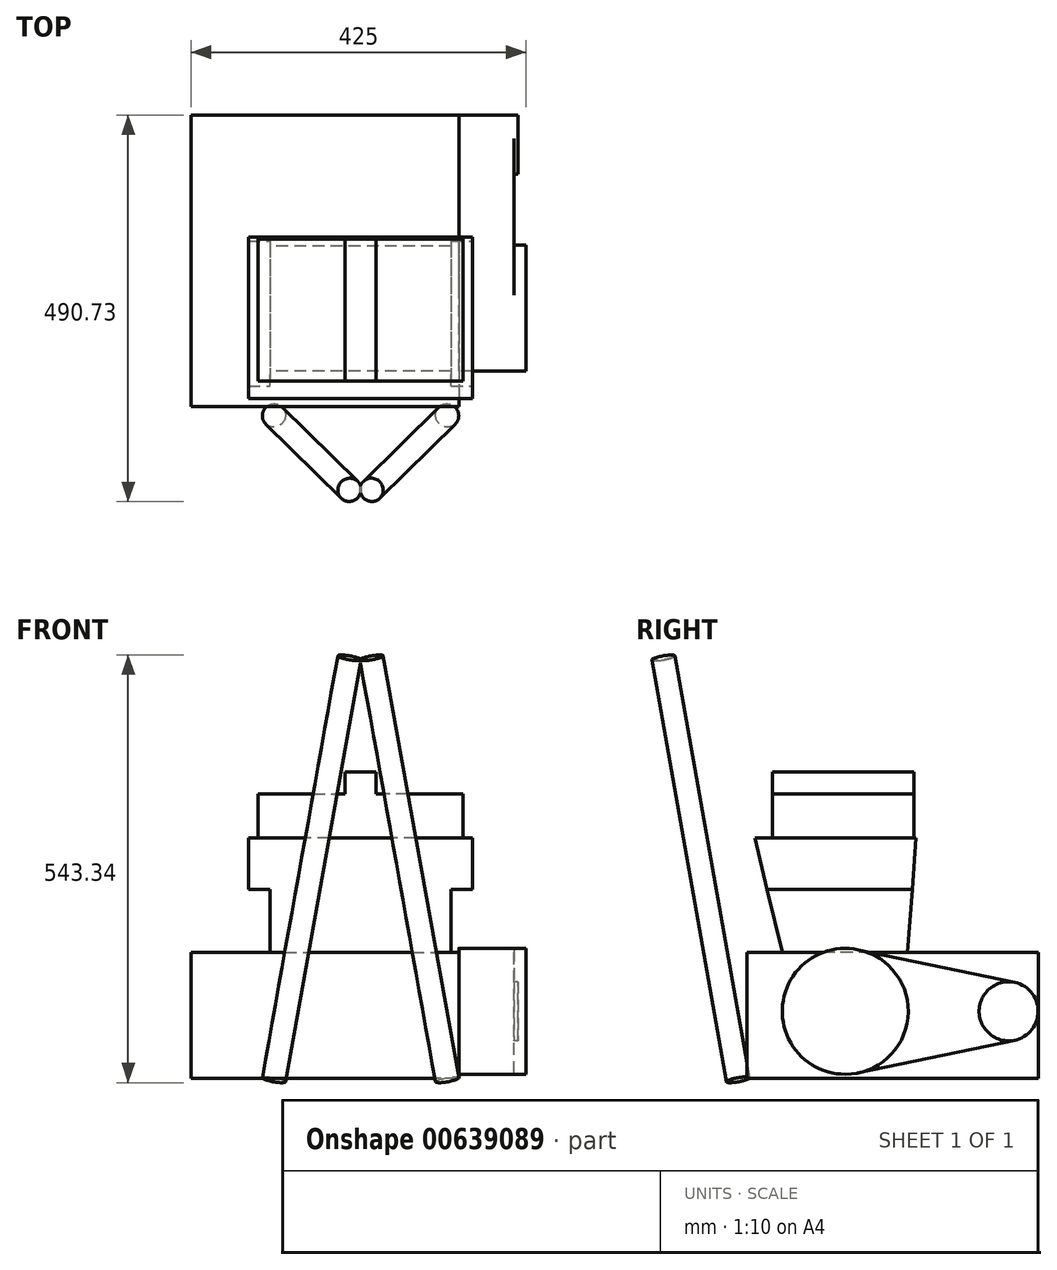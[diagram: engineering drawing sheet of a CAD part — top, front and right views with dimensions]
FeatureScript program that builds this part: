
annotation { "Feature Type Name" : "Feature", "Feature Type Description" : "" }
export const myFeature = defineFeature(function(context is Context, id is Id, definition is map)
    precondition{}
    {
        {
            var Q0;
            Q0=qCreatedBy(makeId("Front.planeOp"),FACE);
            var sketch = newSketch(context, id + "F0", { "sketchPlane" : qUnion([Q0])});
            skLineSegment(sketch, "E0", {"start": v(-215, 0) * mm, "end": v(115, 0) * mm});
            skLineSegment(sketch, "E1", {"start": v(-215, 0) * mm, "end": v(-215, 160) * mm});
            skLineSegment(sketch, "E2", {"start": v(-215, 160) * mm, "end": v(115, 160) * mm});
            skLineSegment(sketch, "E3", {"start": v(-115, 160) * mm, "end": v(-115, 240) * mm});
            skLineSegment(sketch, "E4", {"start": v(115, 160) * mm, "end": v(115, 240) * mm});
            skLineSegment(sketch, "E5", {"start": v(-115, 240) * mm, "end": v(115, 240) * mm});
            skLineSegment(sketch, "E6", {"start": v(-115, 240) * mm, "end": v(-142.5, 240) * mm});
            skLineSegment(sketch, "E7", {"start": v(-142.5, 240) * mm, "end": v(-142.5, 305) * mm});
            skLineSegment(sketch, "E8", {"start": v(-142.5, 305) * mm, "end": v(142.5, 305) * mm});
            skLineSegment(sketch, "E9", {"start": v(142.5, 305) * mm, "end": v(142.5, 240) * mm});
            skLineSegment(sketch, "E10", {"start": v(142.5, 240) * mm, "end": v(115, 240) * mm});
            skLineSegment(sketch, "E11", {"start": v(0, 540.42) * mm, "end": v(0, 0) * mm, "construction": true});
            skLineSegment(sketch, "E12", {"start": v(-130, 305) * mm, "end": v(-130, 361) * mm});
            skLineSegment(sketch, "E13", {"start": v(-20, 389) * mm, "end": v(20, 389) * mm});
            skLineSegment(sketch, "E14", {"start": v(130, 361) * mm, "end": v(130, 305) * mm});
            skLineSegment(sketch, "E15", {"start": v(-130, 361) * mm, "end": v(-20, 361) * mm});
            skLineSegment(sketch, "E16", {"start": v(-20, 361) * mm, "end": v(-20, 389) * mm});
            skLineSegment(sketch, "E17", {"start": v(130, 361) * mm, "end": v(20, 361) * mm});
            skLineSegment(sketch, "E18", {"start": v(20, 361) * mm, "end": v(20, 389) * mm});
            skLineSegment(sketch, "E19", {"start": v(115, 160) * mm, "end": v(115, 0) * mm});
            skLineSegment(sketch, "E20", {"start": v(125, 0) * mm, "end": v(115, 0) * mm});
            skLineSegment(sketch, "E21", {"start": v(115, 160) * mm, "end": v(125, 160) * mm});
            skLineSegment(sketch, "E22", {"start": v(125, 160) * mm, "end": v(125, 0) * mm});
            skSolve(sketch);
        }
        {
            var Q0;
            Q0 = qSketchRegion(id + "F0", true);
            extrude(context, id + "F1", {"entities" : qUnion([Q0]), "oppositeDirection" : true, "depth" : 370 * mm, "offsetDistance" : 25 * mm});
        }
        {
            var Q0;
            Q0=makeQuery(id+"F1.opExtrude","SWEPT_FACE",FACE,{"disambiguationData":[OSD([sQuery(id+"F0.wireOp",EDGE,"E1")])]});
            var sketch = newSketch(context, id + "F2", { "sketchPlane" : qUnion([Q0])});
            skLineSegment(sketch, "E23.10", {"start": v(-370, 160) * mm, "end": v(0, 160) * mm});
            skLineSegment(sketch, "E23.12", {"start": v(-370, 160) * mm, "end": v(0, 160) * mm});
            skLineSegment(sketch, "E23.13", {"start": v(-370, 0) * mm, "end": v(-370, 160) * mm});
            skLineSegment(sketch, "E23.14", {"start": v(-370, 0) * mm, "end": v(0, 0) * mm});
            skLineSegment(sketch, "E23.15", {"start": v(0, 0) * mm, "end": v(0, 160) * mm});
            skLineSegment(sketch, "E24", {"start": v(-165, 160) * mm, "end": v(-165, 507.13) * mm, "construction": true});
            skLineSegment(sketch, "E25", {"start": v(-80, 160) * mm, "end": v(-80, 503.46) * mm, "construction": true});
            skLineSegment(sketch, "E26", {"start": v(-25.69, 240) * mm, "end": v(-210, 240) * mm});
            skLineSegment(sketch, "E27", {"start": v(-215, 305) * mm, "end": v(-10, 305) * mm});
            skLineSegment(sketch, "E28", {"start": v(-203.85, 160) * mm, "end": v(-215, 305) * mm});
            skLineSegment(sketch, "E29", {"start": v(-45, 160) * mm, "end": v(-10, 305) * mm});
            skLineSegment(sketch, "E30", {"start": v(-212.5, 390) * mm, "end": v(-32.5, 390) * mm});
            skLineSegment(sketch, "E31", {"start": v(-212.5, 390) * mm, "end": v(-212.5, 305) * mm});
            skLineSegment(sketch, "E32", {"start": v(-32.5, 390) * mm, "end": v(-32.5, 305) * mm});
            skLineSegment(sketch, "E33", {"start": v(-370, 160) * mm, "end": v(-405.71, 160) * mm});
            skLineSegment(sketch, "E34", {"start": v(-405.71, 160) * mm, "end": v(-405.71, 390) * mm});
            skLineSegment(sketch, "E35", {"start": v(-405.71, 390) * mm, "end": v(-212.5, 390) * mm});
            skLineSegment(sketch, "E36", {"start": v(-32.5, 390) * mm, "end": v(90, 390) * mm});
            skLineSegment(sketch, "E37", {"start": v(90, 390) * mm, "end": v(90, 160) * mm});
            skLineSegment(sketch, "E38", {"start": v(90, 160) * mm, "end": v(0, 160) * mm});
            skLineSegment(sketch, "E39", {"start": v(-25.69, 240) * mm, "end": v(90, 240) * mm, "construction": true});
            skLineSegment(sketch, "E40", {"start": v(-10, 305) * mm, "end": v(90, 305) * mm, "construction": true});
            skLineSegment(sketch, "E41", {"start": v(40, 160) * mm, "end": v(65, 305) * mm, "construction": true});
            skSolve(sketch);
        }
        {
            var Q0;
            {var subQ7=sQuery(id+"F2.wireOp",EDGE,"E31");Q0=makeQuery(id+"F2.imprint","IMPRINT",FACE,{"disambiguationData":[TD([[makeQuery(id+"F2.imprint","IMPRINT",EDGE,{"derivedFrom":subQ7}),-1.0]])]});}
            var Q1;
            {var subQ7=sQuery(id+"F2.wireOp",EDGE,"E32");Q1=makeQuery(id+"F2.imprint","IMPRINT",FACE,{"disambiguationData":[TD([[makeQuery(id+"F2.imprint","IMPRINT",EDGE,{"derivedFrom":subQ7}),1.0]])]});}
            extrude(context, id + "F3", {"entities" : qUnion([Q0, Q1]), "operationType" : NewBodyOperationType.REMOVE, "endBound" : BoundingType.THROUGH_ALL, "oppositeDirection" : true, "depth" : 25 * mm, "offsetDistance" : 25 * mm});
        }
        {
            var Q0;
            {var subQ0=sQuery(id+"F2.wireOp",EDGE,"E23.12");var subQ1=sQuery(id+"F0.wireOp",EDGE,"E2");Q0=makeQuery(id+"F3.boolean.opBoolean","MERGE",FACE,{"derivedFrom":[makeQuery(id+"F1.opExtrude","SWEPT_FACE",FACE,{"disambiguationData":[OSD([subQ1]),TDD([makeQuery(id+"F0.imprint","IMPRINT",EDGE,{"disambiguationData":[TD([[makeQuery(id+"F0.imprint","INTERSECT",VERTEX,{"derivedFrom":[sQuery(id+"F0.wireOp",EDGE,"E1"),subQ1]}),-1.0]])],"derivedFrom":subQ1})])]}),makeQuery(id+"F1.opExtrude","SWEPT_FACE",FACE,{"disambiguationData":[OSD([subQ1]),TDD([makeQuery(id+"F0.imprint","IMPRINT",EDGE,{"disambiguationData":[TD([[makeQuery(id+"F0.imprint","INTERSECT",VERTEX,{"derivedFrom":[subQ1,sQuery(id+"F0.wireOp",EDGE,"ixfZp4do-PrzN-HSM0-8WYw-136xlqfJaLBD")]}),1.0]])],"derivedFrom":subQ1})])]}),makeQuery(id+"F3.opExtrude","SWEPT_FACE",FACE,{"disambiguationData":[OSD([subQ0,sQuery(id+"F2.wireOp",EDGE,"E33")])]}),makeQuery(id+"F3.opExtrude","SWEPT_FACE",FACE,{"disambiguationData":[OSD([subQ0,sQuery(id+"F2.wireOp",EDGE,"E38")])]})]});}
            var sketch = newSketch(context, id + "F4", { "sketchPlane" : qUnion([Q0])});
            skLineSegment(sketch, "E42.0", {"start": v(-215, 0) * mm, "end": v(205, 0) * mm, "construction": true});
            skLineSegment(sketch, "E43", {"start": v(0, 0) * mm, "end": v(0, -40) * mm, "construction": true});
            skLineSegment(sketch, "E44", {"start": v(-143.35, -40) * mm, "end": v(138.45, -40) * mm, "construction": true});
            skSolve(sketch);
        }
        {
            var Q0;
            Q0=sQuery(id+"F4.wireOp",EDGE,"E44");
            cPlane(context, id + "F5", {"entities" : qUnion([Q0]), "cplaneType" : CPlaneType.LINE_ANGLE, "offset" : 40 * mm, "angle" : 10 * degree, "width" : 150 * mm, "height" : 150 * mm});
        }
        {
            var Q0;
            Q0=qCreatedBy(id+"F5.planeOp",FACE);
            var sketch = newSketch(context, id + "F6", { "sketchPlane" : qUnion([Q0])});
            skLineSegment(sketch, "E45", {"start": v(0, 1024.54) * mm, "end": v(0, 0) * mm, "construction": true});
            skLineSegment(sketch, "E46.1", {"start": v(-81.79, 160) * mm, "end": v(0, 160) * mm, "construction": true});
            skLineSegment(sketch, "E47", {"start": v(-110, 0) * mm, "end": v(0, 0) * mm, "construction": true});
            skLineSegment(sketch, "E48", {"start": v(0, 305) * mm, "end": v(-56.22, 305) * mm, "construction": true});
            skLineSegment(sketch, "E49", {"start": v(-110, 0) * mm, "end": v(-56.22, 305) * mm});
            skLineSegment(sketch, "E50", {"start": v(-56.22, 305) * mm, "end": v(0, 623.84) * mm});
            skLineSegment(sketch, "E51.0", {"start": v(-71, 307.6) * mm, "end": v(-14.77, 626.45) * mm});
            skLineSegment(sketch, "E51.1", {"start": v(-124.77, 2.6) * mm, "end": v(-71, 307.6) * mm});
            skLineSegment(sketch, "E52", {"start": v(-14.77, 626.45) * mm, "end": v(0, 623.84) * mm});
            skLineSegment(sketch, "E53", {"start": v(-124.77, 2.6) * mm, "end": v(-110, 0) * mm});
            skLineSegment(sketch, "E54.MirrorCS", {"start": v(14.77, 626.45) * mm, "end": v(0, 623.84) * mm});
            skLineSegment(sketch, "E55.MirrorCS", {"start": v(124.77, 2.6) * mm, "end": v(110, 0) * mm});
            skLineSegment(sketch, "E56.MirrorCS", {"start": v(71, 307.6) * mm, "end": v(14.77, 626.45) * mm});
            skLineSegment(sketch, "E57.MirrorCS", {"start": v(110, 0) * mm, "end": v(56.22, 305) * mm});
            skLineSegment(sketch, "E58.MirrorCS", {"start": v(124.77, 2.6) * mm, "end": v(71, 307.6) * mm});
            skLineSegment(sketch, "E59.MirrorCS", {"start": v(81.79, 160) * mm, "end": v(0, 160) * mm, "construction": true});
            skLineSegment(sketch, "E60.MirrorCS", {"start": v(110, 0) * mm, "end": v(0, 0) * mm, "construction": true});
            skLineSegment(sketch, "E61.MirrorCS", {"start": v(0, 305) * mm, "end": v(56.22, 305) * mm, "construction": true});
            skLineSegment(sketch, "E62.MirrorCS", {"start": v(56.22, 305) * mm, "end": v(0, 623.84) * mm});
            skLineSegment(sketch, "E63", {"start": v(-28.8, 546.9) * mm, "end": v(-14.03, 544.3) * mm});
            skLineSegment(sketch, "E64", {"start": v(14.03, 544.3) * mm, "end": v(28.8, 546.9) * mm});
            skSolve(sketch);
        }
        {
            var Q0;
            {var subQ4=sQuery(id+"F6.wireOp",EDGE,"E49");Q0=makeQuery(id+"F6.imprint","IMPRINT",FACE,{"disambiguationData":[TD([[makeQuery(id+"F6.imprint","IMPRINT",EDGE,{"derivedFrom":subQ4}),1.0]])]});}
            var Q1;
            Q1=sQuery(id+"F6.wireOp",EDGE,"E49");
            revolve(context, id + "F7", {"entities" : qUnion([Q0]), "axis" : qUnion([Q1]), "revolveType" : RevolveType.FULL});
        }
        {
            var Q0;
            Q0=makeQuery(id+"F6.imprint","IMPRINT",FACE,{"disambiguationData":[TD([[makeQuery(id+"F6.imprint","IMPRINT",EDGE,{"derivedFrom":sQuery(id+"F6.wireOp",EDGE,"E55.MirrorCS")}),-1.0]])]});
            var Q1;
            Q1=sQuery(id+"F6.wireOp",EDGE,"E62.MirrorCS");
            revolve(context, id + "F8", {"entities" : qUnion([Q0]), "axis" : qUnion([Q1]), "revolveType" : RevolveType.FULL});
        }
        {
            var Q0;
            Q0=makeQuery(id+"F1.opExtrude","SWEPT_FACE",FACE,{"disambiguationData":[OSD([sQuery(id+"F0.wireOp",EDGE,"E22")])]});
            var sketch = newSketch(context, id + "F9", { "sketchPlane" : qUnion([Q0])});
            skLineSegment(sketch, "E65.0", {"start": v(0, 160) * mm, "end": v(0, 0) * mm});
            skLineSegment(sketch, "E65.1", {"start": v(370, 160) * mm, "end": v(370, 0) * mm});
            skLineSegment(sketch, "E65.2", {"start": v(370, 0) * mm, "end": v(0, 0) * mm});
            skLineSegment(sketch, "E66", {"start": v(0, 160) * mm, "end": v(370, 160) * mm});
            skLineSegment(sketch, "E67", {"start": v(125, 160) * mm, "end": v(125, 0) * mm, "construction": true});
            skCircle(sketch, "E68", {"center": v(125, 85) * mm, "radius": 80 * mm});
            skCircle(sketch, "E69", {"center": v(332.5, 85) * mm, "radius": 37.5 * mm});
            skLineSegment(sketch, "E70", {"start": v(141.39, 163.3) * mm, "end": v(340.18, 121.7) * mm});
            skLineSegment(sketch, "E71", {"start": v(141.39, 6.7) * mm, "end": v(340.18, 48.3) * mm});
            skSolve(sketch);
        }
        {
            var Q0;
            {var subQ0=sQuery(id+"F9.wireOp",EDGE,"E68");var subQ1=sQuery(id+"F9.wireOp",EDGE,"E66");var subQ2=makeQuery(id+"F9.imprint","INTERSECT",VERTEX,{"disambiguationData":[OD(0.0)],"derivedFrom":[subQ1,subQ0]});Q0=makeQuery(id+"F9.imprint","IMPRINT",FACE,{"disambiguationData":[TD([[makeQuery(id+"F9.imprint","IMPRINT",EDGE,{"disambiguationData":[TD([[subQ2,1.0]])],"derivedFrom":subQ1}),1.0]])]});}
            var Q1;
            {var subQ3=sQuery(id+"F9.wireOp",EDGE,"E71");Q1=makeQuery(id+"F9.imprint","IMPRINT",FACE,{"disambiguationData":[TD([[makeQuery(id+"F9.imprint","IMPRINT",EDGE,{"derivedFrom":subQ3}),1.0]])]});}
            var Q2;
            {var subQ0=sQuery(id+"F9.wireOp",EDGE,"E69");var subQ1=makeQuery(id+"F9.imprint","INTERSECT",VERTEX,{"derivedFrom":[subQ0,sQuery(id+"F9.wireOp",EDGE,"E70")]});Q2=makeQuery(id+"F9.imprint","IMPRINT",FACE,{"disambiguationData":[TD([[makeQuery(id+"F9.imprint","IMPRINT",EDGE,{"disambiguationData":[TD([[subQ1,1.0]])],"derivedFrom":subQ0}),1.0]])]});}
            var Q3;
            {var subQ0=sQuery(id+"F9.wireOp",EDGE,"E68");var subQ1=sQuery(id+"F9.wireOp",EDGE,"E66");var subQ2=makeQuery(id+"F9.imprint","INTERSECT",VERTEX,{"disambiguationData":[OD(0.0)],"derivedFrom":[subQ1,subQ0]});Q3=makeQuery(id+"F9.imprint","IMPRINT",FACE,{"disambiguationData":[TD([[makeQuery(id+"F9.imprint","IMPRINT",EDGE,{"disambiguationData":[TD([[subQ2,1.0]])],"derivedFrom":subQ1}),-1.0]])]});}
            var Q4;
            {var subQ0=sQuery(id+"F9.wireOp",EDGE,"E70");var subQ1=sQuery(id+"F9.wireOp",EDGE,"E66");var subQ2=makeQuery(id+"F9.imprint","INTERSECT",VERTEX,{"derivedFrom":[subQ1,subQ0]});Q4=makeQuery(id+"F9.imprint","IMPRINT",FACE,{"disambiguationData":[TD([[makeQuery(id+"F9.imprint","IMPRINT",EDGE,{"disambiguationData":[TD([[subQ2,-1.0]])],"derivedFrom":subQ1}),-1.0]])]});}
            extrude(context, id + "F10", {"entities" : qUnion([Q0, Q1, Q2, Q3, Q4]), "operationType" : NewBodyOperationType.ADD, "depth" : 70 * mm, "offsetDistance" : 25 * mm});
        }
        {
            var Q0;
            Q0=makeQuery(id+"F10.opExtrude","CAP_FACE",FACE,{"disambiguationData":[OSD([sQuery(id+"F9.wireOp",EDGE,"E68"),sQuery(id+"F9.wireOp",EDGE,"E69"),sQuery(id+"F9.wireOp",EDGE,"E70"),sQuery(id+"F9.wireOp",EDGE,"E71")])],"isStart":false});
            var sketch = newSketch(context, id + "F11", { "sketchPlane" : qUnion([Q0])});
            skCircle(sketch, "E72.0", {"center": v(125, 85) * mm, "radius": 80 * mm});
            skCircle(sketch, "E72.1", {"center": v(332.5, 85) * mm, "radius": 37.5 * mm});
            skSolve(sketch);
        }
        {
            var Q0;
            {var subQ0=sQuery(id+"F11.wireOp",EDGE,"E72.0");var subQ1=makeQuery(id+"F11.imprint","INTERSECT",VERTEX,{"derivedFrom":[makeQuery(id+"F10.opExtrude","CAP_EDGE",EDGE,{"disambiguationData":[OSD([sQuery(id+"F9.wireOp",EDGE,"E70")])],"isStart":false}),subQ0]});Q0=makeQuery(id+"F11.imprint","IMPRINT",FACE,{"disambiguationData":[TD([[makeQuery(id+"F11.imprint","IMPRINT",EDGE,{"disambiguationData":[TD([[subQ1,1.0]])],"derivedFrom":subQ0}),1.0]])]});}
            extrude(context, id + "F12", {"entities" : qUnion([Q0]), "operationType" : NewBodyOperationType.ADD, "depth" : 15 * mm, "offsetDistance" : 25 * mm});
        }
        {
            var Q0;
            {var subQ0=sQuery(id+"F11.wireOp",EDGE,"E72.1");var subQ1=makeQuery(id+"F11.imprint","INTERSECT",VERTEX,{"derivedFrom":[makeQuery(id+"F10.opExtrude","CAP_EDGE",EDGE,{"disambiguationData":[OSD([sQuery(id+"F9.wireOp",EDGE,"E70")])],"isStart":false}),subQ0]});Q0=makeQuery(id+"F11.imprint","IMPRINT",FACE,{"disambiguationData":[TD([[makeQuery(id+"F11.imprint","IMPRINT",EDGE,{"disambiguationData":[TD([[subQ1,-1.0]])],"derivedFrom":subQ0}),1.0]])]});}
            extrude(context, id + "F13", {"entities" : qUnion([Q0]), "operationType" : NewBodyOperationType.ADD, "depth" : 5 * mm, "offsetDistance" : 25 * mm});
        }
    });
